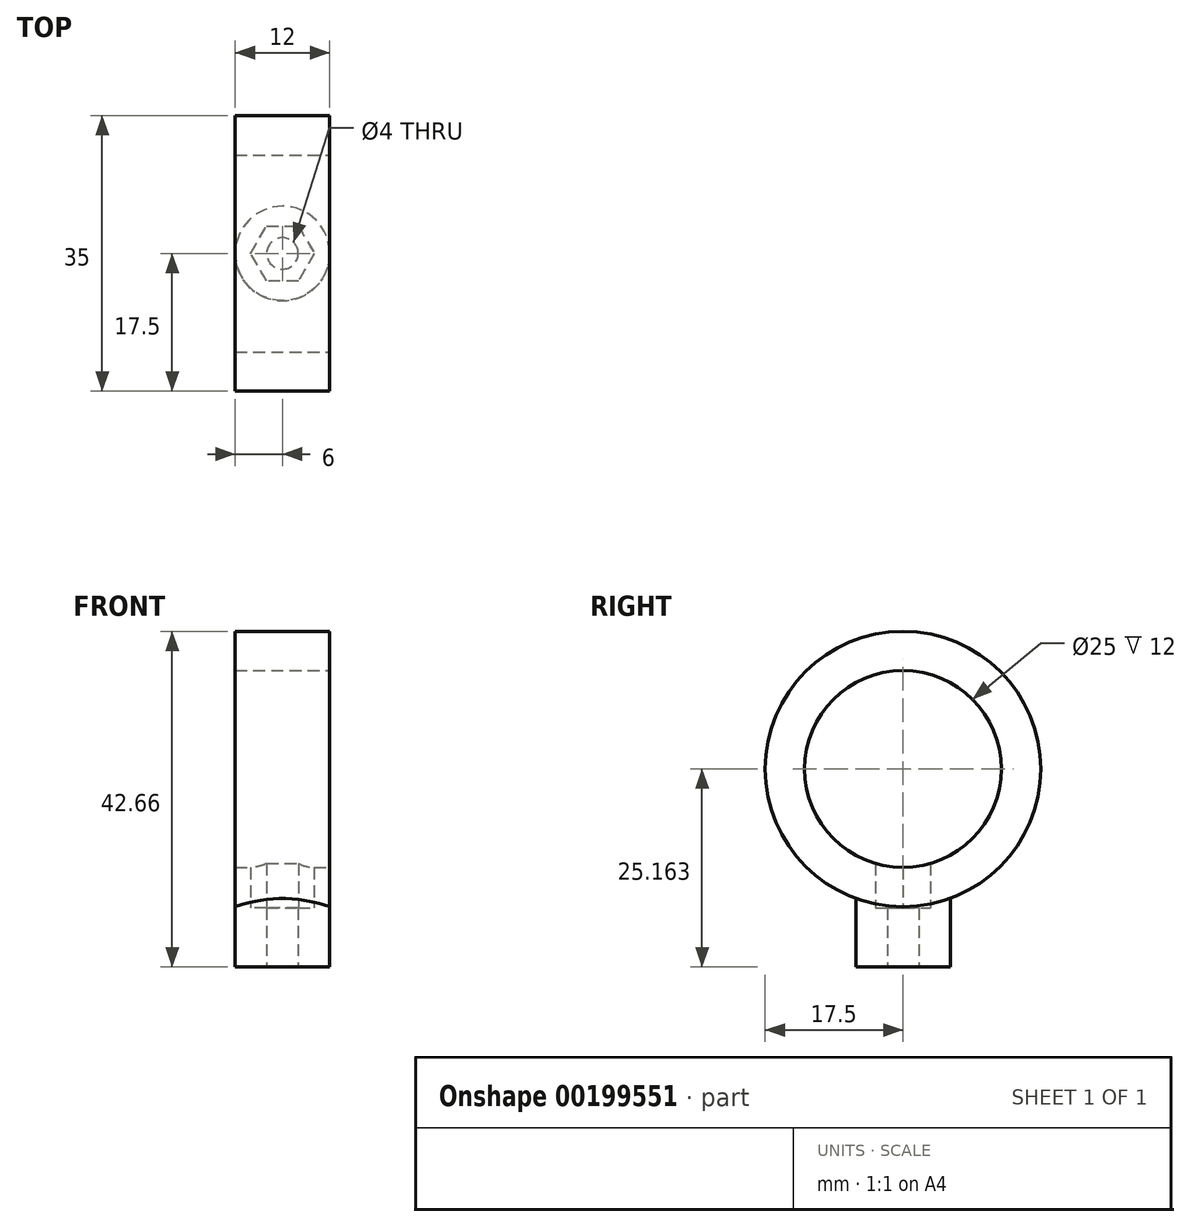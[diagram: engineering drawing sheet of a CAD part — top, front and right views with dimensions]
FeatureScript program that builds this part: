
annotation { "Feature Type Name" : "Feature", "Feature Type Description" : "" }
export const myFeature = defineFeature(function(context is Context, id is Id, definition is map)
    precondition{}
    {
        {
            var Q0;
            Q0=qCreatedBy(makeId("Top.planeOp"),FACE);
            var sketch = newSketch(context, id + "F0", { "sketchPlane" : qUnion([Q0])});
            skCircle(sketch, "E0", {"center": v(0, 0) * mm, "radius": 2 * mm});
            skCircle(sketch, "E1", {"center": v(0, 0) * mm, "radius": 6 * mm});
            skCircle(sketch, "E2.cCircle", {"center": v(0, 0) * mm, "radius": 3.5 * mm, "construction": true});
            skLineSegment(sketch, "E2.0", {"start": v(-2.02, 3.5) * mm, "end": v(2.02, 3.5) * mm});
            skLineSegment(sketch, "E2.1", {"start": v(2.02, 3.5) * mm, "end": v(4.04, 0) * mm});
            skLineSegment(sketch, "E2.2", {"start": v(4.04, 0) * mm, "end": v(2.02, -3.5) * mm});
            skLineSegment(sketch, "E2.3", {"start": v(2.02, -3.5) * mm, "end": v(-2.02, -3.5) * mm});
            skLineSegment(sketch, "E2.4", {"start": v(-2.02, -3.5) * mm, "end": v(-4.04, 0) * mm});
            skLineSegment(sketch, "E2.5", {"start": v(-4.04, 0) * mm, "end": v(-2.02, 3.5) * mm});
            skPoint(sketch, "E2.0.midPoint", {"position": v(0, 3.5) * mm});
            skSolve(sketch);
        }
        {
            var Q0;
            Q0=makeQuery(id+"F0.imprint","IMPRINT",FACE,{"disambiguationData":[TD([[makeQuery(id+"F0.imprint","IMPRINT",EDGE,{"derivedFrom":sQuery(id+"F0.wireOp",EDGE,"E1")}),1.0]])]});
            var Q1;
            Q1=makeQuery(id+"F0.imprint","IMPRINT",FACE,{"disambiguationData":[TD([[makeQuery(id+"F0.imprint","IMPRINT",EDGE,{"derivedFrom":sQuery(id+"F0.wireOp",EDGE,"E0")}),-1.0]])]});
            extrude(context, id + "F1", {"entities" : qUnion([Q0, Q1]), "depth" : 5 * mm});
        }
        {
            var Q0;
            Q0=makeQuery(id+"F1.opExtrude","CAP_FACE",FACE,{"disambiguationData":[OSD([sQuery(id+"F0.wireOp",EDGE,"E0"),sQuery(id+"F0.wireOp",EDGE,"E1")])],"isStart":false});
            var sketch = newSketch(context, id + "F2", { "sketchPlane" : qUnion([Q0])});
            skCircle(sketch, "E3.cCircle", {"center": v(0, 0) * mm, "radius": 3.5 * mm, "construction": true});
            skLineSegment(sketch, "E3.0", {"start": v(1.48, 3.76) * mm, "end": v(4, 0.6) * mm});
            skLineSegment(sketch, "E3.1", {"start": v(4, 0.6) * mm, "end": v(2.51, -3.16) * mm});
            skLineSegment(sketch, "E3.2", {"start": v(2.51, -3.16) * mm, "end": v(-1.48, -3.76) * mm});
            skLineSegment(sketch, "E3.3", {"start": v(-1.48, -3.76) * mm, "end": v(-4, -0.6) * mm});
            skLineSegment(sketch, "E3.4", {"start": v(-4, -0.6) * mm, "end": v(-2.51, 3.16) * mm});
            skLineSegment(sketch, "E3.5", {"start": v(-2.51, 3.16) * mm, "end": v(1.48, 3.76) * mm});
            skPoint(sketch, "E3.0.midPoint", {"position": v(2.74, 2.18) * mm});
            skCircle(sketch, "E4", {"center": v(0, 0) * mm, "radius": 6 * mm});
            skSolve(sketch);
        }
        {
            var Q0;
            Q0 = qSketchRegion(id + "F2", true);
            extrude(context, id + "F3", {"entities" : qUnion([Q0]), "operationType" : NewBodyOperationType.ADD, "depth" : 5 * mm});
        }
        {
            var Q0;
            Q0=qCreatedBy(makeId("Right.planeOp"),FACE);
            var sketch = newSketch(context, id + "F4", { "sketchPlane" : qUnion([Q0])});
            skLineSegment(sketch, "E5", {"start": v(0, 10.16) * mm, "end": v(0, 25.16) * mm});
            skCircle(sketch, "E6", {"center": v(0, 25.16) * mm, "radius": 17.5 * mm});
            skCircle(sketch, "E7", {"center": v(0, 25.16) * mm, "radius": 12.5 * mm});
            skSolve(sketch);
        }
        {
            var Q0;
            Q0 = qSketchRegion(id + "F4", true);
            extrude(context, id + "F5", {"entities" : qUnion([Q0]), "operationType" : NewBodyOperationType.ADD, "oppositeDirection" : true, "depth" : 6 * mm, "hasSecondDirection" : true, "secondDirectionOppositeDirection" : false, "secondDirectionDepth" : 6 * mm});
        }
        {
            var Q0;
            Q0=qCreatedBy(makeId("Top.planeOp"),FACE);
            var sketch = newSketch(context, id + "F6", { "sketchPlane" : qUnion([Q0])});
            skCircle(sketch, "E8", {"center": v(0, 0) * mm, "radius": 6 * mm});
            skSolve(sketch);
        }
        {
            var Q0;
            Q0 = qSketchRegion(id + "F6", true);
            var Q1;
            Q1=makeQuery(id+"F5.opExtrude","SWEPT_FACE",FACE,{"disambiguationData":[OSD([sQuery(id+"F4.wireOp",EDGE,"E7")])]});
            extrude(context, id + "F7", {"entities" : qUnion([Q0]), "operationType" : NewBodyOperationType.ADD, "endBound" : BoundingType.UP_TO_SURFACE, "endBoundEntityFace" : qUnion([Q1]), "depth" : 25 * mm});
        }
        {
            var Q0;
            Q0=makeQuery(id+"F7.boolean.opBoolean","MERGE",FACE,{"derivedFrom":[makeQuery(id+"F1.opExtrude","CAP_FACE",FACE,{"disambiguationData":[OSD([sQuery(id+"F0.wireOp",EDGE,"E0"),sQuery(id+"F0.wireOp",EDGE,"E1")])],"isStart":true}),makeQuery(id+"F7.opExtrude","CAP_FACE",FACE,{"disambiguationData":[OSD([sQuery(id+"F6.wireOp",EDGE,"E8")])],"isStart":true})]});
            var sketch = newSketch(context, id + "F8", { "sketchPlane" : qUnion([Q0])});
            skPoint(sketch, "E9.0.midPoint", {"position": v(2.91, 0) * mm});
            skPoint(sketch, "E9.0.end.orphan", {"position": v(2.91, -1.68) * mm});
            skPoint(sketch, "E10.orphan", {"position": v(2.91, 1.68) * mm});
            skPoint(sketch, "E9.cCircle.center.orphan", {"position": v(0, 0) * mm});
            skCircle(sketch, "E11.cCircle", {"center": v(0, 0) * mm, "radius": 3.5 * mm, "construction": true});
            skLineSegment(sketch, "E11.0", {"start": v(-2.02, 3.5) * mm, "end": v(2.02, 3.5) * mm});
            skLineSegment(sketch, "E11.1", {"start": v(2.02, 3.5) * mm, "end": v(4.04, 0) * mm});
            skLineSegment(sketch, "E11.2", {"start": v(4.04, 0) * mm, "end": v(2.02, -3.5) * mm});
            skLineSegment(sketch, "E11.3", {"start": v(2.02, -3.5) * mm, "end": v(-2.02, -3.5) * mm});
            skLineSegment(sketch, "E11.4", {"start": v(-2.02, -3.5) * mm, "end": v(-4.04, 0) * mm});
            skLineSegment(sketch, "E11.5", {"start": v(-4.04, 0) * mm, "end": v(-2.02, 3.5) * mm});
            skPoint(sketch, "E11.0.midPoint", {"position": v(0, 3.5) * mm});
            skSolve(sketch);
        }
        {
            var Q0;
            Q0 = qSketchRegion(id + "F8", true);
            extrude(context, id + "F9", {"entities" : qUnion([Q0]), "operationType" : NewBodyOperationType.REMOVE, "oppositeDirection" : true, "depth" : 25 * mm});
        }
        {
            var Q0;
            Q0=makeQuery(id+"F7.boolean.opBoolean","MERGE",FACE,{"derivedFrom":[makeQuery(id+"F1.opExtrude","CAP_FACE",FACE,{"disambiguationData":[OSD([sQuery(id+"F0.wireOp",EDGE,"E0"),sQuery(id+"F0.wireOp",EDGE,"E1")])],"isStart":true}),makeQuery(id+"F7.opExtrude","CAP_FACE",FACE,{"disambiguationData":[OSD([sQuery(id+"F6.wireOp",EDGE,"E8")])],"isStart":true})]});
            var sketch = newSketch(context, id + "F10", { "sketchPlane" : qUnion([Q0])});
            skCircle(sketch, "E12", {"center": v(0, 0) * mm, "radius": 2 * mm});
            skCircle(sketch, "E13", {"center": v(0, 0) * mm, "radius": 6 * mm});
            skSolve(sketch);
        }
        {
            var Q0;
            Q0 = qSketchRegion(id + "F10", true);
            extrude(context, id + "F11", {"entities" : qUnion([Q0]), "operationType" : NewBodyOperationType.ADD, "oppositeDirection" : true, "depth" : 7.5 * mm});
        }
    });
